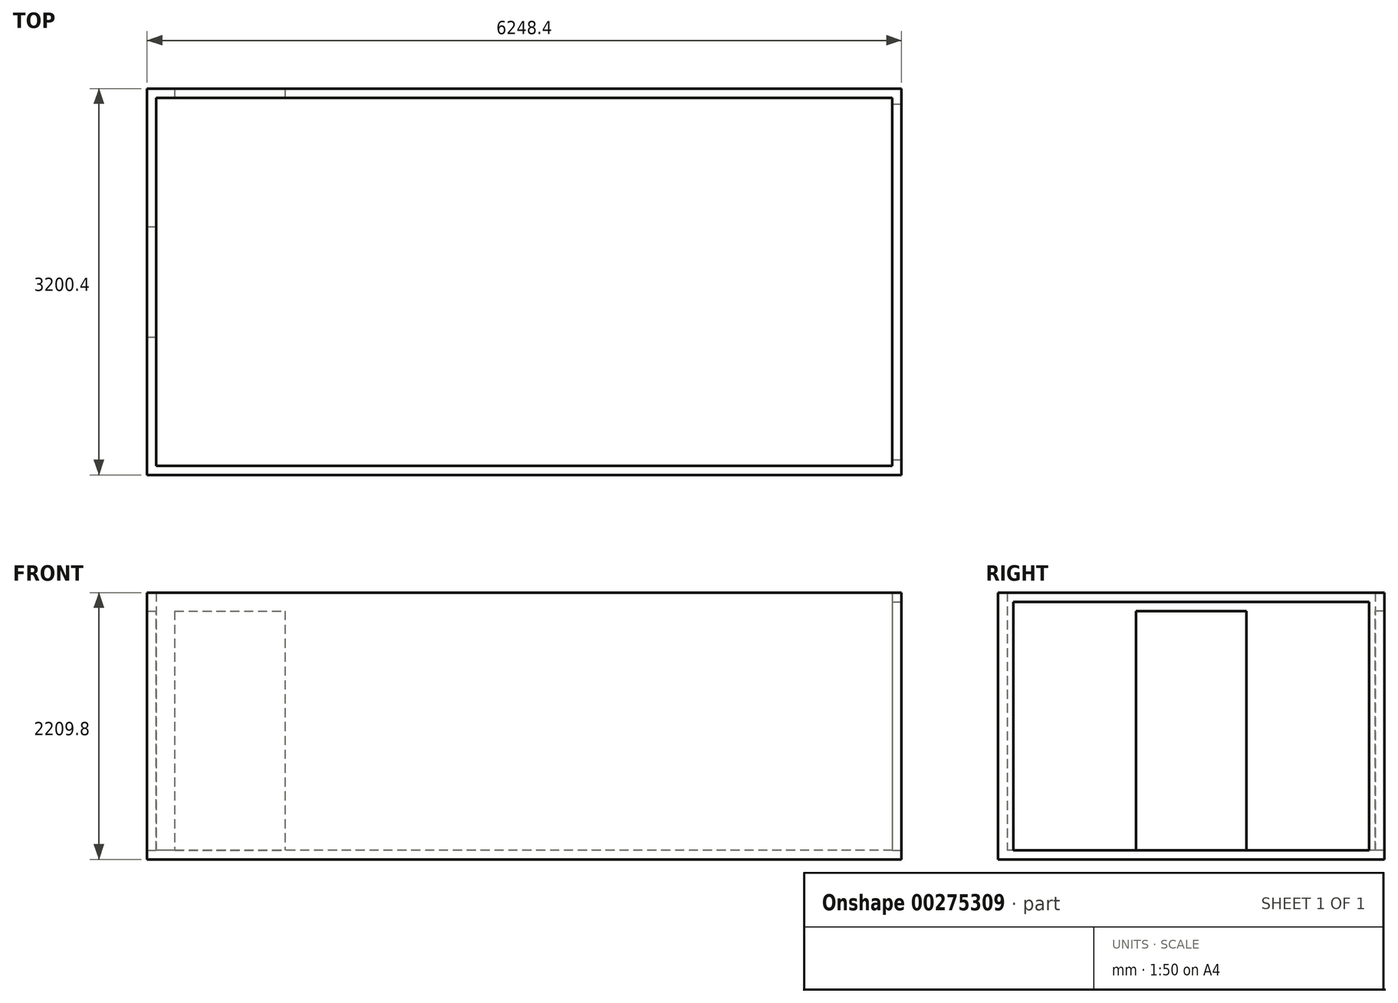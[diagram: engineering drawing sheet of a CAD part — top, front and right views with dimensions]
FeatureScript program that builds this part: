
annotation { "Feature Type Name" : "Feature", "Feature Type Description" : "" }
export const myFeature = defineFeature(function(context is Context, id is Id, definition is map)
    precondition{}
    {
        {
            var Q0;
            Q0=qCreatedBy(makeId("Top.planeOp"),FACE);
            var sketch = newSketch(context, id + "F0", { "sketchPlane" : qUnion([Q0])});
            skLineSegment(sketch, "E0.bottom", {"start": v(3124.2, 1600.2) * mm, "end": v(-3124.2, 1600.2) * mm});
            skLineSegment(sketch, "E0.top", {"start": v(3124.2, -1600.2) * mm, "end": v(-3124.2, -1600.2) * mm});
            skLineSegment(sketch, "E0.left", {"start": v(3124.2, 1600.2) * mm, "end": v(3124.2, -1600.2) * mm});
            skLineSegment(sketch, "E0.right", {"start": v(-3124.2, 1600.2) * mm, "end": v(-3124.2, -1600.2) * mm});
            skPoint(sketch, "E0.middle", {"position": v(0, 0) * mm});
            skSolve(sketch);
        }
        {
            var Q0;
            Q0 = qSketchRegion(id + "F0", true);
            extrude(context, id + "F1", {"entities" : qUnion([Q0]), "depth" : 2209.8 * mm});
        }
        {
            var Q0;
            Q0=makeQuery(id+"F1.opExtrude","CAP_FACE",FACE,{"disambiguationData":[OSD([sQuery(id+"F0.wireOp",EDGE,"E0.bottom"),sQuery(id+"F0.wireOp",EDGE,"E0.top"),sQuery(id+"F0.wireOp",EDGE,"E0.left"),sQuery(id+"F0.wireOp",EDGE,"E0.right")])],"isStart":false});
            shell(context, id + "F2", {"entities" : qUnion([Q0]), "thickness" : 76.2 * mm});
        }
        {
            var Q0;
            Q0=makeQuery(id+"F2.opShell","OFFSET_FACE",FACE,{"disambiguationData":[OSD([sQuery(id+"F0.wireOp",EDGE,"E0.right")])]});
            var sketch = newSketch(context, id + "F3", { "sketchPlane" : qUnion([Q0])});
            skLineSegment(sketch, "E1.bottom", {"start": v(-457.2, 76.2) * mm, "end": v(457.2, 76.2) * mm});
            skLineSegment(sketch, "E1.top", {"start": v(-457.2, 2057.4) * mm, "end": v(457.2, 2057.4) * mm});
            skLineSegment(sketch, "E1.left", {"start": v(-457.2, 76.2) * mm, "end": v(-457.2, 2057.4) * mm});
            skLineSegment(sketch, "E1.right", {"start": v(457.2, 76.2) * mm, "end": v(457.2, 2057.4) * mm});
            skPoint(sketch, "E1.middle", {"position": v(0, 1066.8) * mm});
            skPoint(sketch, "E1.middle.positionSnap0", {"position": v(0, 76.2) * mm});
            skPoint(sketch, "E1.centerSnap0", {"position": v(0, 76.2) * mm});
            skLineSegment(sketch, "E2", {"start": v(0, 2057.4) * mm, "end": v(0, 76.2) * mm, "construction": true});
            skSolve(sketch);
        }
        {
            var Q0;
            Q0 = qSketchRegion(id + "F3", true);
            extrude(context, id + "F4", {"entities" : qUnion([Q0]), "operationType" : NewBodyOperationType.REMOVE, "endBound" : BoundingType.UP_TO_NEXT, "oppositeDirection" : true, "depth" : 25.4 * mm});
        }
        {
            var Q0;
            Q0=makeQuery(id+"F1.opExtrude","SWEPT_FACE",FACE,{"disambiguationData":[OSD([sQuery(id+"F0.wireOp",EDGE,"E0.left")])]});
            var sketch = newSketch(context, id + "F5", { "sketchPlane" : qUnion([Q0])});
            skLineSegment(sketch, "E3", {"start": v(0, 0) * mm, "end": v(0, 2209.8) * mm, "construction": true});
            skLineSegment(sketch, "E4.bottom", {"start": v(-1473.2, 76.2) * mm, "end": v(1473.2, 76.2) * mm});
            skLineSegment(sketch, "E4.top", {"start": v(-1473.2, 2133.6) * mm, "end": v(1473.2, 2133.6) * mm});
            skLineSegment(sketch, "E4.left", {"start": v(-1473.2, 76.2) * mm, "end": v(-1473.2, 2133.6) * mm});
            skLineSegment(sketch, "E4.right", {"start": v(1473.2, 76.2) * mm, "end": v(1473.2, 2133.6) * mm});
            skPoint(sketch, "E4.middle", {"position": v(0, 1104.9) * mm});
            skSolve(sketch);
        }
        {
            var Q0;
            Q0 = qSketchRegion(id + "F5", true);
            extrude(context, id + "F6", {"entities" : qUnion([Q0]), "operationType" : NewBodyOperationType.REMOVE, "endBound" : BoundingType.UP_TO_NEXT, "oppositeDirection" : true, "depth" : 25.4 * mm});
        }
        {
            var Q0;
            Q0=makeQuery(id+"F2.opShell","OFFSET_FACE",FACE,{"disambiguationData":[OSD([sQuery(id+"F0.wireOp",EDGE,"E0.bottom")])]});
            var sketch = newSketch(context, id + "F7", { "sketchPlane" : qUnion([Q0])});
            skLineSegment(sketch, "E5", {"start": v(-2438.4, 2209.8) * mm, "end": v(-2438.4, 76.2) * mm, "construction": true});
            skLineSegment(sketch, "E6.bottom", {"start": v(-1981.2, 76.2) * mm, "end": v(-2895.6, 76.2) * mm});
            skLineSegment(sketch, "E6.top", {"start": v(-1981.2, 2057.4) * mm, "end": v(-2895.6, 2057.4) * mm});
            skLineSegment(sketch, "E6.left", {"start": v(-1981.2, 76.2) * mm, "end": v(-1981.2, 2057.4) * mm});
            skLineSegment(sketch, "E6.right", {"start": v(-2895.6, 76.2) * mm, "end": v(-2895.6, 2057.4) * mm});
            skPoint(sketch, "E6.middle", {"position": v(-2438.4, 1066.8) * mm});
            skSolve(sketch);
        }
        {
            var Q0;
            Q0 = qSketchRegion(id + "F7", true);
            extrude(context, id + "F8", {"entities" : qUnion([Q0]), "operationType" : NewBodyOperationType.REMOVE, "endBound" : BoundingType.UP_TO_NEXT, "oppositeDirection" : true, "depth" : 25.4 * mm});
        }
    });
